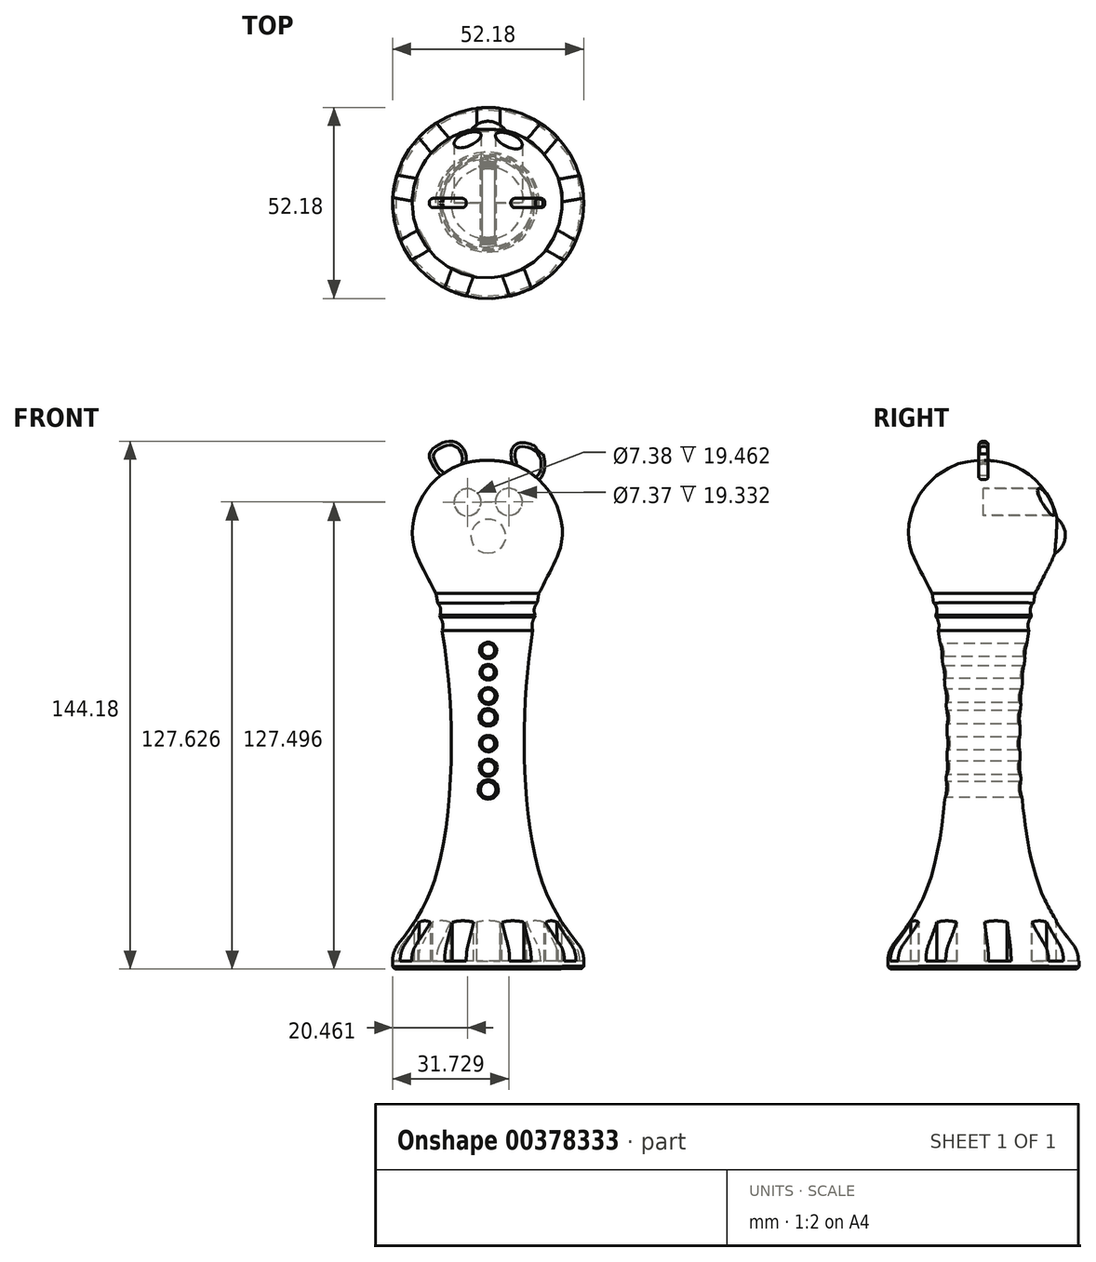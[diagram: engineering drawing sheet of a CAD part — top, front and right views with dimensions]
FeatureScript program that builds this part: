
annotation { "Feature Type Name" : "Feature", "Feature Type Description" : "" }
export const myFeature = defineFeature(function(context is Context, id is Id, definition is map)
    precondition{}
    {
        {
            var Q0;
            Q0=qCreatedBy(makeId("Front.planeOp"),FACE);
            var sketch = newSketch(context, id + "F0", { "sketchPlane" : qUnion([Q0])});
            skLineSegment(sketch, "E0", {"start": v(0, -66.9) * mm, "end": v(-25.47, -66.9) * mm});
            skLineSegment(sketch, "E1", {"start": v(-25.47, -66.9) * mm, "end": v(-26.09, -66.26) * mm});
            skLineSegment(sketch, "E2", {"start": v(-26.09, -66.26) * mm, "end": v(-26.09, -62) * mm});
            skFitSpline(sketch, "E3", {"points": [v(-26.09, -62) * mm, v(-14.72, -42.8) * mm, v(-10.24, 3.42) * mm, v(-14.25, 35.7) * mm], "startDerivative": vector(46.73, 58.31) * mm, "endDerivative": vector(-14.97, 88.45) * mm});
            skLineSegment(sketch, "E4", {"start": v(-14.25, 35.7) * mm, "end": v(-14.25, 41.6) * mm});
            skFitSpline(sketch, "E5", {"points": [v(-14.25, 35.7) * mm, v(-17.03, 41.06) * mm, v(-20.57, 49.98) * mm, v(-17.59, 62.89) * mm, v(-6.43, 71.33) * mm, v(0, 71.96) * mm], "startDerivative": vector(-19.32, 32.18) * mm, "endDerivative": vector(5.1, -2.57) * mm});
            skArc(sketch, "E6", {"start": v(-13.24, 29.75) * mm, "mid": v(-13, 31.52) * mm, "end": v(-13.8, 33.1) * mm});
            skFitSpline(sketch, "E7", {"points": [v(-13.16, 29.24) * mm, v(-12.88, 28.88) * mm, v(-12.46, 27.75) * mm, v(-12.33, 26.7) * mm, v(-12.56, 25.56) * mm], "startDerivative": vector(1.65, -1.65) * mm, "endDerivative": vector(-1.13, -4.18) * mm});
            skLineSegment(sketch, "E8", {"start": v(-0.28, 72.1) * mm, "end": v(0, -66.9) * mm});
            skSolve(sketch);
        }
        {
            var Q0;
            {var subQ3=sQuery(id+"F0.wireOp",EDGE,"E0");Q0=makeQuery(id+"F0.imprint","IMPRINT",FACE,{"disambiguationData":[TD([[makeQuery(id+"F0.imprint","IMPRINT",EDGE,{"derivedFrom":subQ3}),-1.0]])]});}
            var Q1;
            Q1=sQuery(id+"F0.wireOp",EDGE,"E8");
            revolve(context, id + "F1", {"entities" : qUnion([Q0]), "axis" : qUnion([Q1]), "revolveType" : RevolveType.FULL});
        }
        {
            var Q0;
            Q0=qCreatedBy(makeId("Top.planeOp"),FACE);
            var sketch = newSketch(context, id + "F2", { "sketchPlane" : qUnion([Q0])});
            skLineSegment(sketch, "E9.bottom", {"start": v(-3.06, 26.92) * mm, "end": v(3.2, 26.92) * mm});
            skLineSegment(sketch, "E9.top", {"start": v(-3.06, 19.93) * mm, "end": v(3.2, 19.93) * mm});
            skLineSegment(sketch, "E9.left", {"start": v(-3.06, 26.92) * mm, "end": v(-3.06, 19.93) * mm});
            skLineSegment(sketch, "E9.right", {"start": v(3.2, 26.92) * mm, "end": v(3.2, 19.93) * mm});
            skLineSegment(sketch, "E10.1.0", {"start": v(-14.84, 22.68) * mm, "end": v(-10.36, 17.33) * mm});
            skLineSegment(sketch, "E10.1.1", {"start": v(-19.65, 18.65) * mm, "end": v(-14.84, 22.68) * mm});
            skLineSegment(sketch, "E10.1.2", {"start": v(-19.65, 18.65) * mm, "end": v(-15.16, 13.3) * mm});
            skLineSegment(sketch, "E10.1.3", {"start": v(-15.16, 13.3) * mm, "end": v(-10.36, 17.33) * mm});
            skLineSegment(sketch, "E10.2.0", {"start": v(-25.95, 7.83) * mm, "end": v(-19.07, 6.62) * mm});
            skLineSegment(sketch, "E10.2.1", {"start": v(-27.04, 1.66) * mm, "end": v(-25.95, 7.83) * mm});
            skLineSegment(sketch, "E10.2.2", {"start": v(-27.04, 1.66) * mm, "end": v(-20.16, 0.45) * mm});
            skLineSegment(sketch, "E10.2.3", {"start": v(-20.16, 0.45) * mm, "end": v(-19.07, 6.62) * mm});
            skLineSegment(sketch, "E10.3.0", {"start": v(-24.91, -10.68) * mm, "end": v(-18.87, -7.19) * mm});
            skLineSegment(sketch, "E10.3.1", {"start": v(-21.78, -16.1) * mm, "end": v(-24.91, -10.68) * mm});
            skLineSegment(sketch, "E10.3.2", {"start": v(-21.78, -16.1) * mm, "end": v(-15.73, -12.62) * mm});
            skLineSegment(sketch, "E10.3.3", {"start": v(-15.73, -12.62) * mm, "end": v(-18.87, -7.19) * mm});
            skLineSegment(sketch, "E10.4.0", {"start": v(-12.22, -24.2) * mm, "end": v(-9.83, -17.63) * mm});
            skLineSegment(sketch, "E10.4.1", {"start": v(-6.33, -26.34) * mm, "end": v(-12.22, -24.2) * mm});
            skLineSegment(sketch, "E10.4.2", {"start": v(-6.33, -26.34) * mm, "end": v(-3.94, -19.78) * mm});
            skLineSegment(sketch, "E10.4.3", {"start": v(-3.94, -19.78) * mm, "end": v(-9.83, -17.63) * mm});
            skLineSegment(sketch, "E10.5.0", {"start": v(6.2, -26.4) * mm, "end": v(3.8, -19.83) * mm});
            skLineSegment(sketch, "E10.5.1", {"start": v(12.08, -24.25) * mm, "end": v(6.2, -26.4) * mm});
            skLineSegment(sketch, "E10.5.2", {"start": v(12.08, -24.25) * mm, "end": v(9.7, -17.68) * mm});
            skLineSegment(sketch, "E10.5.3", {"start": v(9.7, -17.68) * mm, "end": v(3.8, -19.83) * mm});
            skLineSegment(sketch, "E10.6.0", {"start": v(21.7, -16.24) * mm, "end": v(15.66, -12.75) * mm});
            skLineSegment(sketch, "E10.6.1", {"start": v(24.84, -10.8) * mm, "end": v(21.7, -16.24) * mm});
            skLineSegment(sketch, "E10.6.2", {"start": v(24.84, -10.8) * mm, "end": v(18.8, -7.32) * mm});
            skLineSegment(sketch, "E10.6.3", {"start": v(18.8, -7.32) * mm, "end": v(15.66, -12.75) * mm});
            skLineSegment(sketch, "E10.7.0", {"start": v(27.07, 1.51) * mm, "end": v(20.19, 0.3) * mm});
            skLineSegment(sketch, "E10.7.1", {"start": v(25.98, 7.69) * mm, "end": v(27.07, 1.51) * mm});
            skLineSegment(sketch, "E10.7.2", {"start": v(25.98, 7.69) * mm, "end": v(19.1, 6.48) * mm});
            skLineSegment(sketch, "E10.7.3", {"start": v(19.1, 6.48) * mm, "end": v(20.19, 0.3) * mm});
            skLineSegment(sketch, "E10.8.0", {"start": v(19.76, 18.56) * mm, "end": v(15.27, 13.2) * mm});
            skLineSegment(sketch, "E10.8.1", {"start": v(14.96, 22.59) * mm, "end": v(19.76, 18.56) * mm});
            skLineSegment(sketch, "E10.8.2", {"start": v(14.96, 22.59) * mm, "end": v(10.47, 17.24) * mm});
            skLineSegment(sketch, "E10.8.3", {"start": v(10.47, 17.24) * mm, "end": v(15.27, 13.2) * mm});
            skPoint(sketch, "E10.center", {"position": v(0, 0) * mm});
            skSolve(sketch);
        }
        {
            var Q0;
            Q0 = qSketchRegion(id + "F2", true);
            extrude(context, id + "F3", {"entities" : qUnion([Q0]), "operationType" : NewBodyOperationType.REMOVE, "oppositeDirection" : true, "depth" : 64.73 * mm});
        }
        {
            var Q0;
            {var subQ0=sQuery(id+"F0.wireOp",EDGE,"E2");var subQ1=sQuery(id+"F0.wireOp",EDGE,"E3");Q0=makeQuery(id+"F3.boolean.opBoolean","SPLIT",EDGE,{"disambiguationData":[TD([makeQuery(id+"F3.opExtrude","SWEPT_FACE",FACE,{"disambiguationData":[OSD([sQuery(id+"F2.wireOp",EDGE,"E10.1.2")])]})])],"derivedFrom":makeQuery(id+"F1.opRevolve","SWEPT_EDGE",EDGE,{"disambiguationData":[OSD([subQ0,subQ1])]})});}
            var Q1;
            {var subQ0=sQuery(id+"F0.wireOp",EDGE,"E2");var subQ1=sQuery(id+"F0.wireOp",EDGE,"E3");Q1=makeQuery(id+"F3.boolean.opBoolean","SPLIT",EDGE,{"disambiguationData":[TD([makeQuery(id+"F3.opExtrude","SWEPT_FACE",FACE,{"disambiguationData":[OSD([sQuery(id+"F2.wireOp",EDGE,"E10.2.2")])]})])],"derivedFrom":makeQuery(id+"F1.opRevolve","SWEPT_EDGE",EDGE,{"disambiguationData":[OSD([subQ0,subQ1])]})});}
            var Q2;
            {var subQ0=sQuery(id+"F0.wireOp",EDGE,"E2");var subQ1=sQuery(id+"F0.wireOp",EDGE,"E3");Q2=makeQuery(id+"F3.boolean.opBoolean","SPLIT",EDGE,{"disambiguationData":[TD([makeQuery(id+"F3.opExtrude","SWEPT_FACE",FACE,{"disambiguationData":[OSD([sQuery(id+"F2.wireOp",EDGE,"E10.3.2")])]})])],"derivedFrom":makeQuery(id+"F1.opRevolve","SWEPT_EDGE",EDGE,{"disambiguationData":[OSD([subQ0,subQ1])]})});}
            var Q3;
            {var subQ0=sQuery(id+"F0.wireOp",EDGE,"E2");var subQ1=sQuery(id+"F0.wireOp",EDGE,"E3");Q3=makeQuery(id+"F3.boolean.opBoolean","SPLIT",EDGE,{"disambiguationData":[TD([makeQuery(id+"F3.opExtrude","SWEPT_FACE",FACE,{"disambiguationData":[OSD([sQuery(id+"F2.wireOp",EDGE,"E9.left")])]})])],"derivedFrom":makeQuery(id+"F1.opRevolve","SWEPT_EDGE",EDGE,{"disambiguationData":[OSD([subQ0,subQ1])]})});}
            var Q4;
            {var subQ0=sQuery(id+"F0.wireOp",EDGE,"E2");var subQ1=sQuery(id+"F0.wireOp",EDGE,"E3");Q4=makeQuery(id+"F3.boolean.opBoolean","SPLIT",EDGE,{"disambiguationData":[TD([makeQuery(id+"F3.opExtrude","SWEPT_FACE",FACE,{"disambiguationData":[OSD([sQuery(id+"F2.wireOp",EDGE,"E9.right")])]})])],"derivedFrom":makeQuery(id+"F1.opRevolve","SWEPT_EDGE",EDGE,{"disambiguationData":[OSD([subQ0,subQ1])]})});}
            var Q5;
            {var subQ0=sQuery(id+"F0.wireOp",EDGE,"E2");var subQ1=sQuery(id+"F0.wireOp",EDGE,"E3");Q5=makeQuery(id+"F3.boolean.opBoolean","SPLIT",EDGE,{"disambiguationData":[TD([makeQuery(id+"F3.opExtrude","SWEPT_FACE",FACE,{"disambiguationData":[OSD([sQuery(id+"F2.wireOp",EDGE,"E10.7.2")])]})])],"derivedFrom":makeQuery(id+"F1.opRevolve","SWEPT_EDGE",EDGE,{"disambiguationData":[OSD([subQ0,subQ1])]})});}
            var Q6;
            {var subQ0=sQuery(id+"F0.wireOp",EDGE,"E2");var subQ1=sQuery(id+"F0.wireOp",EDGE,"E3");Q6=makeQuery(id+"F3.boolean.opBoolean","SPLIT",EDGE,{"disambiguationData":[TD([makeQuery(id+"F3.opExtrude","SWEPT_FACE",FACE,{"disambiguationData":[OSD([sQuery(id+"F2.wireOp",EDGE,"E10.6.2")])]})])],"derivedFrom":makeQuery(id+"F1.opRevolve","SWEPT_EDGE",EDGE,{"disambiguationData":[OSD([subQ0,subQ1])]})});}
            var Q7;
            {var subQ0=sQuery(id+"F0.wireOp",EDGE,"E2");var subQ1=sQuery(id+"F0.wireOp",EDGE,"E3");Q7=makeQuery(id+"F3.boolean.opBoolean","SPLIT",EDGE,{"disambiguationData":[TD([makeQuery(id+"F3.opExtrude","SWEPT_FACE",FACE,{"disambiguationData":[OSD([sQuery(id+"F2.wireOp",EDGE,"E10.5.2")])]})])],"derivedFrom":makeQuery(id+"F1.opRevolve","SWEPT_EDGE",EDGE,{"disambiguationData":[OSD([subQ0,subQ1])]})});}
            var Q8;
            {var subQ0=sQuery(id+"F0.wireOp",EDGE,"E2");var subQ1=sQuery(id+"F0.wireOp",EDGE,"E3");Q8=makeQuery(id+"F3.boolean.opBoolean","SPLIT",EDGE,{"disambiguationData":[TD([makeQuery(id+"F3.opExtrude","SWEPT_FACE",FACE,{"disambiguationData":[OSD([sQuery(id+"F2.wireOp",EDGE,"E10.4.2")])]})])],"derivedFrom":makeQuery(id+"F1.opRevolve","SWEPT_EDGE",EDGE,{"disambiguationData":[OSD([subQ0,subQ1])]})});}
            fillet(context, id + "F4", {"entities" : qUnion([Q0, Q1, Q2, Q3, Q4, Q5, Q6, Q7, Q8]), "radius" : 7.18 * mm, "tangentPropagation" : true, "allowEdgeOverflow" : false});
        }
        {
            var Q0;
            Q0=qCreatedBy(makeId("Front.planeOp"),FACE);
            var sketch = newSketch(context, id + "F5", { "sketchPlane" : qUnion([Q0])});
            skCircle(sketch, "E11", {"center": v(-5.63, 60.6) * mm, "radius": 3.69 * mm});
            skLineSegment(sketch, "E12", {"start": v(0, 74.32) * mm, "end": v(0, 44.55) * mm});
            skSolve(sketch);
        }
        {
            var Q0;
            Q0 = qSketchRegion(id + "F5", true);
            extrude(context, id + "F6", {"entities" : qUnion([Q0]), "operationType" : NewBodyOperationType.REMOVE, "oppositeDirection" : true, "depth" : 127 * mm});
        }
        {
            var Q0;
            Q0=qCreatedBy(makeId("Front.planeOp"),FACE);
            var sketch = newSketch(context, id + "F7", { "sketchPlane" : qUnion([Q0])});
            skCircle(sketch, "E13", {"center": v(5.64, 60.74) * mm, "radius": 3.68 * mm});
            skSolve(sketch);
        }
        {
            var Q0;
            Q0 = qSketchRegion(id + "F7", true);
            extrude(context, id + "F8", {"entities" : qUnion([Q0]), "operationType" : NewBodyOperationType.REMOVE, "oppositeDirection" : true, "depth" : 127 * mm});
        }
        {
            var Q0;
            Q0=qCreatedBy(makeId("Front.planeOp"),FACE);
            var sketch = newSketch(context, id + "F9", { "sketchPlane" : qUnion([Q0])});
            skFitSpline(sketch, "E14", {"points": [v(-11.6, 67.3) * mm, v(-12.95, 67.92) * mm, v(-14.26, 69.31) * mm, v(-15.07, 70.63) * mm, v(-16.02, 72.89) * mm, v(-15.07, 75.28) * mm, v(-9.24, 77.15) * mm, v(-6.02, 72.89) * mm, v(-5.94, 70.05) * mm, v(4.63, 69.8) * mm, v(6.63, 70.88) * mm, v(6.23, 73.47) * mm, v(7.97, 76.64) * mm, v(13.91, 75.16) * mm, v(15.44, 70.5) * mm, v(12.09, 65.93) * mm, v(-11.6, 67.3) * mm]});
            skSolve(sketch);
        }
        {
            var Q0;
            Q0=makeQuery(id+"F9.imprint","IMPRINT",FACE,{"disambiguationData":[TD([[makeQuery(id+"F9.imprint","IMPRINT",EDGE,{"derivedFrom":sQuery(id+"F9.wireOp",EDGE,"E14")}),-1.0]])]});
            extrude(context, id + "F10", {"entities" : qUnion([Q0]), "operationType" : NewBodyOperationType.ADD, "endBound" : BoundingType.SYMMETRIC, "depth" : 2.54 * mm});
        }
        {
            var Q0;
            Q0=makeQuery(id+"F10.boolean.opBoolean","SPLIT",EDGE,{"disambiguationData":[OD(0.0)],"derivedFrom":makeQuery(id+"F10.opExtrude","CAP_EDGE",EDGE,{"disambiguationData":[OSD([sQuery(id+"F9.wireOp",EDGE,"E14")])],"isStart":false})});
            var Q1;
            Q1=makeQuery(id+"F10.boolean.opBoolean","SPLIT",EDGE,{"disambiguationData":[OD(1.0)],"derivedFrom":makeQuery(id+"F10.opExtrude","CAP_EDGE",EDGE,{"disambiguationData":[OSD([sQuery(id+"F9.wireOp",EDGE,"E14")])],"isStart":false})});
            var Q2;
            Q2=makeQuery(id+"F10.boolean.opBoolean","SPLIT",EDGE,{"disambiguationData":[OD(0.0)],"derivedFrom":makeQuery(id+"F10.opExtrude","CAP_EDGE",EDGE,{"disambiguationData":[OSD([sQuery(id+"F9.wireOp",EDGE,"E14")])],"isStart":true})});
            var Q3;
            Q3=makeQuery(id+"F10.boolean.opBoolean","SPLIT",EDGE,{"disambiguationData":[OD(1.0)],"derivedFrom":makeQuery(id+"F10.opExtrude","CAP_EDGE",EDGE,{"disambiguationData":[OSD([sQuery(id+"F9.wireOp",EDGE,"E14")])],"isStart":true})});
            fillet(context, id + "F11", {"entities" : qUnion([Q0, Q1, Q2, Q3]), "radius" : 1.04 * mm, "tangentPropagation" : true, "allowEdgeOverflow" : false});
        }
        {
            var Q0;
            Q0=qCreatedBy(makeId("Front.planeOp"),FACE);
            var sketch = newSketch(context, id + "F12", { "sketchPlane" : qUnion([Q0])});
            skCircle(sketch, "E15", {"center": v(0, 20.21) * mm, "radius": 1.76 * mm});
            skCircle(sketch, "E16", {"center": v(0, 14.23) * mm, "radius": 1.68 * mm});
            skCircle(sketch, "E17", {"center": v(0, 7.74) * mm, "radius": 1.83 * mm});
            skCircle(sketch, "E18", {"center": v(0, 1.9) * mm, "radius": 1.9 * mm});
            skCircle(sketch, "E19", {"center": v(0, -5.3) * mm, "radius": 1.76 * mm});
            skCircle(sketch, "E20", {"center": v(0, -11.89) * mm, "radius": 1.84 * mm});
            skCircle(sketch, "E21", {"center": v(0, -17.87) * mm, "radius": 2.15 * mm});
            skLineSegment(sketch, "E22", {"start": v(0, 37.05) * mm, "end": v(0, -43.86) * mm});
            skSolve(sketch);
        }
        {
            var Q0;
            Q0 = qSketchRegion(id + "F12", true);
            extrude(context, id + "F13", {"entities" : qUnion([Q0]), "operationType" : NewBodyOperationType.REMOVE, "endBound" : BoundingType.SYMMETRIC, "oppositeDirection" : true, "depth" : 127 * mm});
        }
        {
            var Q0;
            {var subQ0=sQuery(id+"F0.wireOp",EDGE,"E3");Q0=makeQuery(id+"F13.boolean.opBoolean","INTERSECT",EDGE,{"disambiguationData":[OD(1.0)],"derivedFrom":[makeQuery(id+"F1.opRevolve","SWEPT_FACE",FACE,{"disambiguationData":[OSD([subQ0]),TDD([makeQuery(id+"F0.imprint","IMPRINT",EDGE,{"disambiguationData":[TD([[makeQuery(id+"F0.imprint","INTERSECT",VERTEX,{"derivedFrom":[sQuery(id+"F0.wireOp",EDGE,"E2"),subQ0]}),-1.0]])],"derivedFrom":subQ0})])]}),makeQuery(id+"F13.opExtrude","SWEPT_FACE",FACE,{"disambiguationData":[OSD([sQuery(id+"F12.wireOp",EDGE,"E15")])]})]});}
            var Q1;
            {var subQ0=sQuery(id+"F0.wireOp",EDGE,"E3");Q1=makeQuery(id+"F13.boolean.opBoolean","INTERSECT",EDGE,{"disambiguationData":[OD(1.0)],"derivedFrom":[makeQuery(id+"F1.opRevolve","SWEPT_FACE",FACE,{"disambiguationData":[OSD([subQ0]),TDD([makeQuery(id+"F0.imprint","IMPRINT",EDGE,{"disambiguationData":[TD([[makeQuery(id+"F0.imprint","INTERSECT",VERTEX,{"derivedFrom":[sQuery(id+"F0.wireOp",EDGE,"E2"),subQ0]}),-1.0]])],"derivedFrom":subQ0})])]}),makeQuery(id+"F13.opExtrude","SWEPT_FACE",FACE,{"disambiguationData":[OSD([sQuery(id+"F12.wireOp",EDGE,"E16")])]})]});}
            var Q2;
            {var subQ0=sQuery(id+"F0.wireOp",EDGE,"E3");Q2=makeQuery(id+"F13.boolean.opBoolean","INTERSECT",EDGE,{"disambiguationData":[OD(1.0)],"derivedFrom":[makeQuery(id+"F1.opRevolve","SWEPT_FACE",FACE,{"disambiguationData":[OSD([subQ0]),TDD([makeQuery(id+"F0.imprint","IMPRINT",EDGE,{"disambiguationData":[TD([[makeQuery(id+"F0.imprint","INTERSECT",VERTEX,{"derivedFrom":[sQuery(id+"F0.wireOp",EDGE,"E2"),subQ0]}),-1.0]])],"derivedFrom":subQ0})])]}),makeQuery(id+"F13.opExtrude","SWEPT_FACE",FACE,{"disambiguationData":[OSD([sQuery(id+"F12.wireOp",EDGE,"E17")])]})]});}
            var Q3;
            {var subQ0=sQuery(id+"F0.wireOp",EDGE,"E3");Q3=makeQuery(id+"F13.boolean.opBoolean","INTERSECT",EDGE,{"disambiguationData":[OD(1.0)],"derivedFrom":[makeQuery(id+"F1.opRevolve","SWEPT_FACE",FACE,{"disambiguationData":[OSD([subQ0]),TDD([makeQuery(id+"F0.imprint","IMPRINT",EDGE,{"disambiguationData":[TD([[makeQuery(id+"F0.imprint","INTERSECT",VERTEX,{"derivedFrom":[sQuery(id+"F0.wireOp",EDGE,"E2"),subQ0]}),-1.0]])],"derivedFrom":subQ0})])]}),makeQuery(id+"F13.opExtrude","SWEPT_FACE",FACE,{"disambiguationData":[OSD([sQuery(id+"F12.wireOp",EDGE,"E18")])]})]});}
            var Q4;
            {var subQ0=sQuery(id+"F0.wireOp",EDGE,"E3");Q4=makeQuery(id+"F13.boolean.opBoolean","INTERSECT",EDGE,{"disambiguationData":[OD(1.0)],"derivedFrom":[makeQuery(id+"F1.opRevolve","SWEPT_FACE",FACE,{"disambiguationData":[OSD([subQ0]),TDD([makeQuery(id+"F0.imprint","IMPRINT",EDGE,{"disambiguationData":[TD([[makeQuery(id+"F0.imprint","INTERSECT",VERTEX,{"derivedFrom":[sQuery(id+"F0.wireOp",EDGE,"E2"),subQ0]}),-1.0]])],"derivedFrom":subQ0})])]}),makeQuery(id+"F13.opExtrude","SWEPT_FACE",FACE,{"disambiguationData":[OSD([sQuery(id+"F12.wireOp",EDGE,"E19")])]})]});}
            var Q5;
            {var subQ0=sQuery(id+"F0.wireOp",EDGE,"E3");Q5=makeQuery(id+"F13.boolean.opBoolean","INTERSECT",EDGE,{"disambiguationData":[OD(1.0)],"derivedFrom":[makeQuery(id+"F1.opRevolve","SWEPT_FACE",FACE,{"disambiguationData":[OSD([subQ0]),TDD([makeQuery(id+"F0.imprint","IMPRINT",EDGE,{"disambiguationData":[TD([[makeQuery(id+"F0.imprint","INTERSECT",VERTEX,{"derivedFrom":[sQuery(id+"F0.wireOp",EDGE,"E2"),subQ0]}),-1.0]])],"derivedFrom":subQ0})])]}),makeQuery(id+"F13.opExtrude","SWEPT_FACE",FACE,{"disambiguationData":[OSD([sQuery(id+"F12.wireOp",EDGE,"E20")])]})]});}
            var Q6;
            {var subQ0=sQuery(id+"F0.wireOp",EDGE,"E3");Q6=makeQuery(id+"F13.boolean.opBoolean","INTERSECT",EDGE,{"disambiguationData":[OD(1.0)],"derivedFrom":[makeQuery(id+"F1.opRevolve","SWEPT_FACE",FACE,{"disambiguationData":[OSD([subQ0]),TDD([makeQuery(id+"F0.imprint","IMPRINT",EDGE,{"disambiguationData":[TD([[makeQuery(id+"F0.imprint","INTERSECT",VERTEX,{"derivedFrom":[sQuery(id+"F0.wireOp",EDGE,"E2"),subQ0]}),-1.0]])],"derivedFrom":subQ0})])]}),makeQuery(id+"F13.opExtrude","SWEPT_FACE",FACE,{"disambiguationData":[OSD([sQuery(id+"F12.wireOp",EDGE,"E21")])]})]});}
            var Q7;
            {var subQ0=sQuery(id+"F0.wireOp",EDGE,"E3");Q7=makeQuery(id+"F13.boolean.opBoolean","INTERSECT",EDGE,{"disambiguationData":[OD(0.0)],"derivedFrom":[makeQuery(id+"F1.opRevolve","SWEPT_FACE",FACE,{"disambiguationData":[OSD([subQ0]),TDD([makeQuery(id+"F0.imprint","IMPRINT",EDGE,{"disambiguationData":[TD([[makeQuery(id+"F0.imprint","INTERSECT",VERTEX,{"derivedFrom":[sQuery(id+"F0.wireOp",EDGE,"E2"),subQ0]}),-1.0]])],"derivedFrom":subQ0})])]}),makeQuery(id+"F13.opExtrude","SWEPT_FACE",FACE,{"disambiguationData":[OSD([sQuery(id+"F12.wireOp",EDGE,"E15")])]})]});}
            var Q8;
            {var subQ0=sQuery(id+"F0.wireOp",EDGE,"E3");Q8=makeQuery(id+"F13.boolean.opBoolean","INTERSECT",EDGE,{"disambiguationData":[OD(0.0)],"derivedFrom":[makeQuery(id+"F1.opRevolve","SWEPT_FACE",FACE,{"disambiguationData":[OSD([subQ0]),TDD([makeQuery(id+"F0.imprint","IMPRINT",EDGE,{"disambiguationData":[TD([[makeQuery(id+"F0.imprint","INTERSECT",VERTEX,{"derivedFrom":[sQuery(id+"F0.wireOp",EDGE,"E2"),subQ0]}),-1.0]])],"derivedFrom":subQ0})])]}),makeQuery(id+"F13.opExtrude","SWEPT_FACE",FACE,{"disambiguationData":[OSD([sQuery(id+"F12.wireOp",EDGE,"E16")])]})]});}
            var Q9;
            {var subQ0=sQuery(id+"F0.wireOp",EDGE,"E3");Q9=makeQuery(id+"F13.boolean.opBoolean","INTERSECT",EDGE,{"disambiguationData":[OD(0.0)],"derivedFrom":[makeQuery(id+"F1.opRevolve","SWEPT_FACE",FACE,{"disambiguationData":[OSD([subQ0]),TDD([makeQuery(id+"F0.imprint","IMPRINT",EDGE,{"disambiguationData":[TD([[makeQuery(id+"F0.imprint","INTERSECT",VERTEX,{"derivedFrom":[sQuery(id+"F0.wireOp",EDGE,"E2"),subQ0]}),-1.0]])],"derivedFrom":subQ0})])]}),makeQuery(id+"F13.opExtrude","SWEPT_FACE",FACE,{"disambiguationData":[OSD([sQuery(id+"F12.wireOp",EDGE,"E17")])]})]});}
            var Q10;
            {var subQ0=sQuery(id+"F0.wireOp",EDGE,"E3");Q10=makeQuery(id+"F13.boolean.opBoolean","INTERSECT",EDGE,{"disambiguationData":[OD(0.0)],"derivedFrom":[makeQuery(id+"F1.opRevolve","SWEPT_FACE",FACE,{"disambiguationData":[OSD([subQ0]),TDD([makeQuery(id+"F0.imprint","IMPRINT",EDGE,{"disambiguationData":[TD([[makeQuery(id+"F0.imprint","INTERSECT",VERTEX,{"derivedFrom":[sQuery(id+"F0.wireOp",EDGE,"E2"),subQ0]}),-1.0]])],"derivedFrom":subQ0})])]}),makeQuery(id+"F13.opExtrude","SWEPT_FACE",FACE,{"disambiguationData":[OSD([sQuery(id+"F12.wireOp",EDGE,"E18")])]})]});}
            var Q11;
            {var subQ0=sQuery(id+"F0.wireOp",EDGE,"E3");Q11=makeQuery(id+"F13.boolean.opBoolean","INTERSECT",EDGE,{"disambiguationData":[OD(0.0)],"derivedFrom":[makeQuery(id+"F1.opRevolve","SWEPT_FACE",FACE,{"disambiguationData":[OSD([subQ0]),TDD([makeQuery(id+"F0.imprint","IMPRINT",EDGE,{"disambiguationData":[TD([[makeQuery(id+"F0.imprint","INTERSECT",VERTEX,{"derivedFrom":[sQuery(id+"F0.wireOp",EDGE,"E2"),subQ0]}),-1.0]])],"derivedFrom":subQ0})])]}),makeQuery(id+"F13.opExtrude","SWEPT_FACE",FACE,{"disambiguationData":[OSD([sQuery(id+"F12.wireOp",EDGE,"E19")])]})]});}
            var Q12;
            {var subQ0=sQuery(id+"F0.wireOp",EDGE,"E3");Q12=makeQuery(id+"F13.boolean.opBoolean","INTERSECT",EDGE,{"disambiguationData":[OD(0.0)],"derivedFrom":[makeQuery(id+"F1.opRevolve","SWEPT_FACE",FACE,{"disambiguationData":[OSD([subQ0]),TDD([makeQuery(id+"F0.imprint","IMPRINT",EDGE,{"disambiguationData":[TD([[makeQuery(id+"F0.imprint","INTERSECT",VERTEX,{"derivedFrom":[sQuery(id+"F0.wireOp",EDGE,"E2"),subQ0]}),-1.0]])],"derivedFrom":subQ0})])]}),makeQuery(id+"F13.opExtrude","SWEPT_FACE",FACE,{"disambiguationData":[OSD([sQuery(id+"F12.wireOp",EDGE,"E20")])]})]});}
            var Q13;
            {var subQ0=sQuery(id+"F0.wireOp",EDGE,"E3");Q13=makeQuery(id+"F13.boolean.opBoolean","INTERSECT",EDGE,{"disambiguationData":[OD(0.0)],"derivedFrom":[makeQuery(id+"F1.opRevolve","SWEPT_FACE",FACE,{"disambiguationData":[OSD([subQ0]),TDD([makeQuery(id+"F0.imprint","IMPRINT",EDGE,{"disambiguationData":[TD([[makeQuery(id+"F0.imprint","INTERSECT",VERTEX,{"derivedFrom":[sQuery(id+"F0.wireOp",EDGE,"E2"),subQ0]}),-1.0]])],"derivedFrom":subQ0})])]}),makeQuery(id+"F13.opExtrude","SWEPT_FACE",FACE,{"disambiguationData":[OSD([sQuery(id+"F12.wireOp",EDGE,"E21")])]})]});}
            fillet(context, id + "F14", {"entities" : qUnion([Q0, Q1, Q2, Q3, Q4, Q5, Q6, Q7, Q8, Q9, Q10, Q11, Q12, Q13]), "radius" : 0.48 * mm, "tangentPropagation" : true, "allowEdgeOverflow" : false});
        }
        {
            var Q0;
            Q0=qCreatedBy(makeId("Front.planeOp"),FACE);
            var sketch = newSketch(context, id + "F15", { "sketchPlane" : qUnion([Q0])});
            skFitSpline(sketch, "E23", {"points": [v(13.01, 76.47) * mm, v(13.03, 75.52) * mm, v(13.86, 74.46) * mm, v(14.67, 73.85) * mm, v(16.13, 73.97) * mm], "startDerivative": vector(-0.7, -4.27) * mm, "endDerivative": vector(5.8, 1.25) * mm});
            skLineSegment(sketch, "E24", {"start": v(13.01, 76.47) * mm, "end": v(16.13, 73.97) * mm});
            skSolve(sketch);
        }
        {
            var Q0;
            Q0 = qSketchRegion(id + "F15", true);
            extrude(context, id + "F16", {"entities" : qUnion([Q0]), "operationType" : NewBodyOperationType.REMOVE, "endBound" : BoundingType.SYMMETRIC, "oppositeDirection" : true, "depth" : 25.4 * mm});
        }
        {
            var Q0;
            Q0=qCreatedBy(makeId("Right.planeOp"),FACE);
            var sketch = newSketch(context, id + "F17", { "sketchPlane" : qUnion([Q0])});
            skCircle(sketch, "E25", {"center": v(16.62, 51.58) * mm, "radius": 5.72 * mm});
            skLineSegment(sketch, "E26", {"start": v(16.62, 51.58) * mm, "end": v(16.62, 39.82) * mm});
            skLineSegment(sketch, "E27", {"start": v(16.62, 51.58) * mm, "end": v(16.62, 66.69) * mm});
            skSolve(sketch);
        }
        {
            var Q0;
            {var subQ0=sQuery(id+"F17.wireOp",EDGE,"E26");var subQ1=sQuery(id+"F17.wireOp",EDGE,"E25");var subQ2=makeQuery(id+"F17.imprint","INTERSECT",VERTEX,{"derivedFrom":[subQ1,subQ0]});Q0=makeQuery(id+"F17.imprint","IMPRINT",FACE,{"disambiguationData":[TD([[makeQuery(id+"F17.imprint","IMPRINT",EDGE,{"disambiguationData":[TD([[subQ2,-1.0]])],"derivedFrom":subQ1}),1.0]])]});}
            var Q1;
            Q1=sQuery(id+"F17.wireOp",EDGE,"E25");
            var Q2;
            Q2=sQuery(id+"F17.wireOp",EDGE,"E26");
            revolve(context, id + "F18", {"operationType" : NewBodyOperationType.ADD, "entities" : qUnion([Q0]), "surfaceEntities" : qUnion([Q1]), "axis" : qUnion([Q2]), "revolveType" : RevolveType.FULL});
        }
    });
